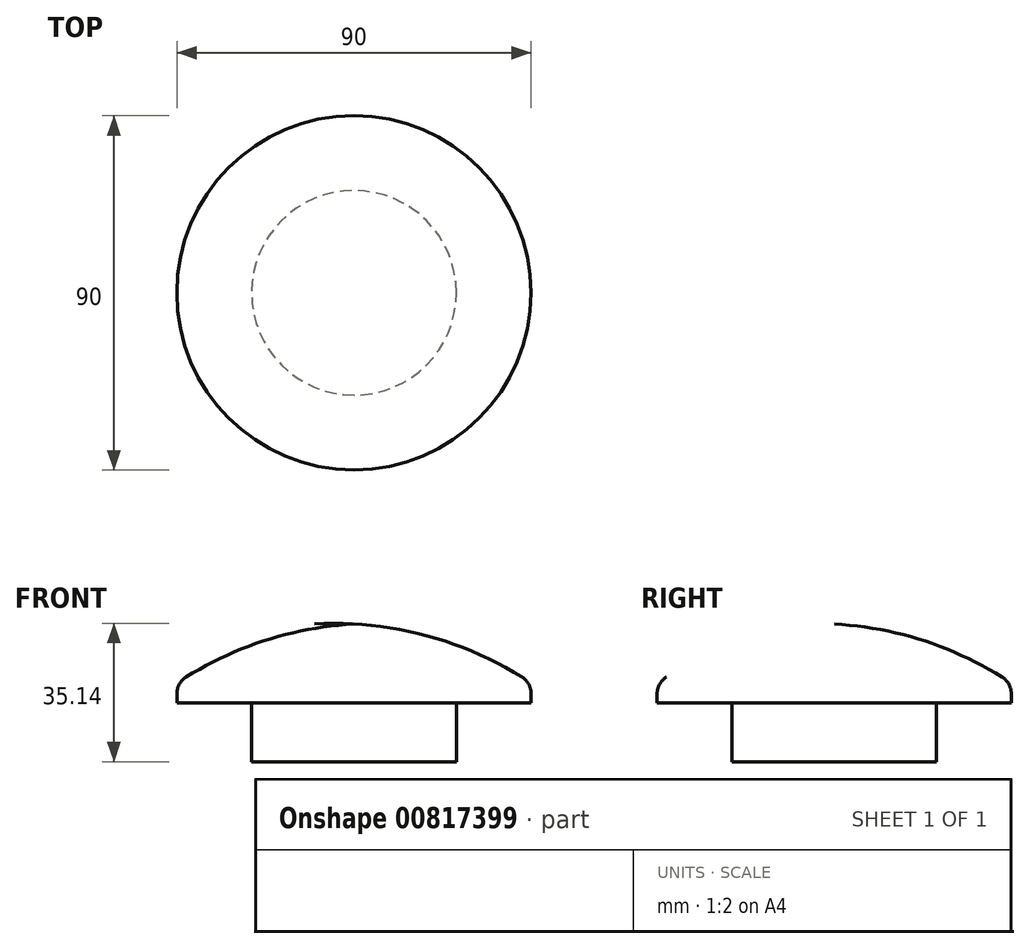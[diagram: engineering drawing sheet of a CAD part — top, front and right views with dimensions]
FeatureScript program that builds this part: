
annotation { "Feature Type Name" : "Feature", "Feature Type Description" : "" }
export const myFeature = defineFeature(function(context is Context, id is Id, definition is map)
    precondition{}
    {
        {
            var Q0;
            Q0=qCreatedBy(makeId("Top.planeOp"),FACE);
            var sketch = newSketch(context, id + "F0", { "sketchPlane" : qUnion([Q0])});
            skCircle(sketch, "E0", {"center": v(0, 0) * mm, "radius": 26 * mm});
            skSolve(sketch);
        }
        {
            var Q0;
            Q0 = qSketchRegion(id + "F0", true);
            extrude(context, id + "F1", {"entities" : qUnion([Q0]), "depth" : 15 * mm, "offsetDistance" : 25 * mm});
        }
        {
            var Q0;
            Q0=qCreatedBy(makeId("Right.planeOp"),FACE);
            var sketch = newSketch(context, id + "F2", { "sketchPlane" : qUnion([Q0])});
            skLineSegment(sketch, "E1", {"start": v(0, 15) * mm, "end": v(-45, 15) * mm});
            skLineSegment(sketch, "E2", {"start": v(-45, 15) * mm, "end": v(-45, 20) * mm});
            skLineSegment(sketch, "E3", {"start": v(0, 35) * mm, "end": v(0, 15) * mm});
            skArc(sketch, "E4", {"start": v(0, 35) * mm, "mid": v(-23.5, 30.51) * mm, "end": v(-45, 20) * mm});
            skLineSegment(sketch, "E5", {"start": v(0, -35.5) * mm, "end": v(0, 110.19) * mm, "construction": true});
            skSolve(sketch);
        }
        {
            var Q0;
            Q0 = qSketchRegion(id + "F2", true);
            var Q1;
            Q1=sQuery(id+"F2.wireOp",EDGE,"E5");
            revolve(context, id + "F3", {"operationType" : NewBodyOperationType.ADD, "surfaceOperationType" : NewSurfaceOperationType.NEW, "entities" : qUnion([Q0]), "axis" : qUnion([Q1]), "revolveType" : RevolveType.FULL});
        }
        {
            var Q0;
            Q0=makeQuery(id+"F3.opRevolve","SWEPT_EDGE",EDGE,{"disambiguationData":[OSD([sQuery(id+"F2.wireOp",EDGE,"E2"),sQuery(id+"F2.wireOp",EDGE,"E4")])]});
            fillet(context, id + "F4", {"entities" : qUnion([Q0]), "radius" : 5 * mm, "tangentPropagation" : true, "allowEdgeOverflow" : false});
        }
    });
